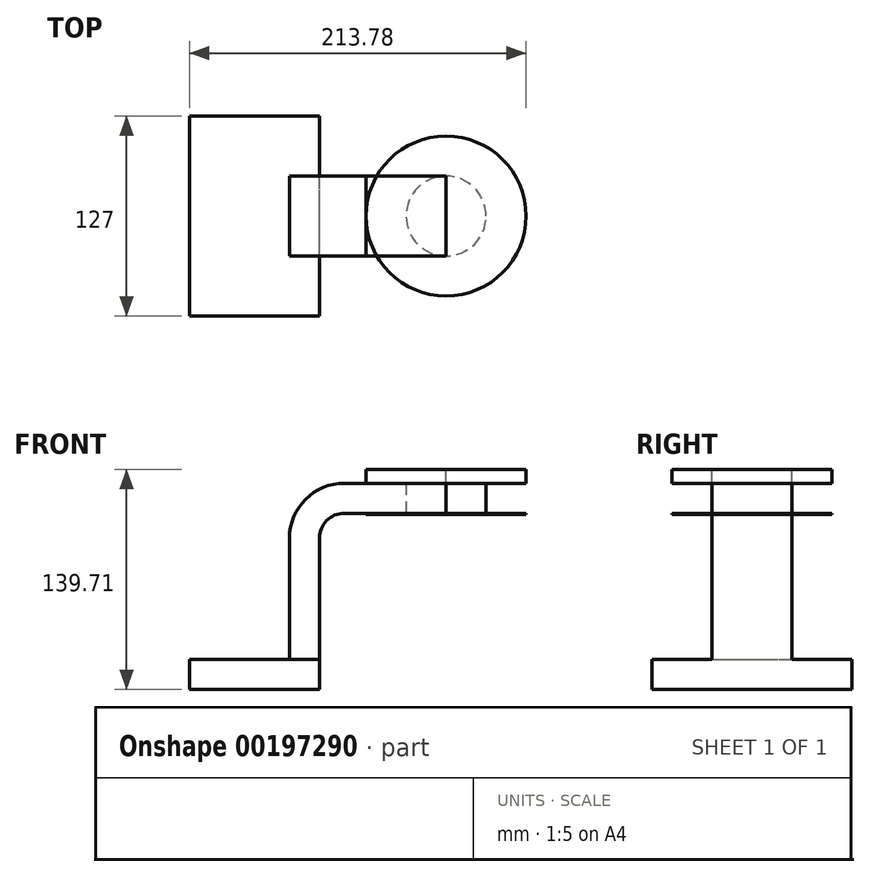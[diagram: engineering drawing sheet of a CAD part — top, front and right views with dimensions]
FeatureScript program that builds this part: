
annotation { "Feature Type Name" : "Feature", "Feature Type Description" : "" }
export const myFeature = defineFeature(function(context is Context, id is Id, definition is map)
    precondition{}
    {
        {
            var Q0;
            Q0=qCreatedBy(makeId("Front.planeOp"),FACE);
            var sketch = newSketch(context, id + "F0", { "sketchPlane" : qUnion([Q0])});
            skLineSegment(sketch, "E0.bottom", {"start": v(41.27, 9.53) * mm, "end": v(-41.27, 9.53) * mm});
            skLineSegment(sketch, "E0.top", {"start": v(41.28, -9.52) * mm, "end": v(-41.27, -9.52) * mm});
            skLineSegment(sketch, "E0.left", {"start": v(41.27, 9.53) * mm, "end": v(41.28, -9.52) * mm});
            skLineSegment(sketch, "E0.right", {"start": v(-41.27, 9.53) * mm, "end": v(-41.27, -9.52) * mm});
            skPoint(sketch, "E0.middle", {"position": v(0, 0) * mm});
            skLineSegment(sketch, "E1.bottom", {"start": v(121.7, 101.6) * mm, "end": v(70.9, 101.6) * mm});
            skLineSegment(sketch, "E1.top", {"start": v(121.7, 130.18) * mm, "end": v(70.9, 130.18) * mm});
            skLineSegment(sketch, "E1.left", {"start": v(121.7, 101.6) * mm, "end": v(121.7, 130.18) * mm});
            skLineSegment(sketch, "E1.right", {"start": v(70.9, 101.6) * mm, "end": v(70.9, 130.18) * mm});
            skPoint(sketch, "E1.middle", {"position": v(96.3, 115.89) * mm});
            skLineSegment(sketch, "E2", {"start": v(41.27, 9.53) * mm, "end": v(41.27, 86.54) * mm});
            skArc(sketch, "E3", {"start": v(41.27, 86.54) * mm, "mid": v(45.92, 97.77) * mm, "end": v(57.15, 102.42) * mm});
            skLineSegment(sketch, "E4", {"start": v(57.15, 102.42) * mm, "end": v(96.3, 102.42) * mm});
            skLineSegment(sketch, "E5.0", {"start": v(57.15, 121.47) * mm, "end": v(96.3, 121.47) * mm});
            skArc(sketch, "E5.1", {"start": v(22.22, 86.54) * mm, "mid": v(32.45, 111.24) * mm, "end": v(57.15, 121.47) * mm});
            skLineSegment(sketch, "E5.2", {"start": v(22.22, 9.53) * mm, "end": v(22.22, 86.54) * mm});
            skLineSegment(sketch, "E6", {"start": v(96.3, 121.47) * mm, "end": v(96.3, 102.42) * mm});
            skFitSpline(sketch, "E7", {"points": [v(-41.28, 9.53) * mm, v(57.15, 121.47) * mm], "startDerivative": vector(0.72, 245.98) * mm, "endDerivative": vector(63.18, -1.79) * mm});
            skSolve(sketch);
        }
        {
            var Q0;
            Q0=makeQuery(id+"F0.imprint","IMPRINT",FACE,{"disambiguationData":[TD([[makeQuery(id+"F0.imprint","IMPRINT",EDGE,{"derivedFrom":sQuery(id+"F0.wireOp",EDGE,"E0.top")}),-1.0]])]});
            extrude(context, id + "F1", {"entities" : qUnion([Q0]), "endBound" : BoundingType.SYMMETRIC, "depth" : 127 * mm});
        }
        {
            var Q0;
            {var subQ1=sQuery(id+"F0.wireOp",EDGE,"E2");Q0=makeQuery(id+"F0.imprint","IMPRINT",FACE,{"disambiguationData":[TD([[makeQuery(id+"F0.imprint","IMPRINT",EDGE,{"derivedFrom":subQ1}),1.0]])]});}
            var Q1;
            {var subQ1=sQuery(id+"F0.wireOp",EDGE,"E1.bottom");Q1=makeQuery(id+"F0.imprint","IMPRINT",FACE,{"disambiguationData":[TD([[makeQuery(id+"F0.imprint","IMPRINT",EDGE,{"derivedFrom":subQ1}),-1.0]])]});}
            var Q2;
            {var subQ5=sQuery(id+"F0.wireOp",EDGE,"E6");Q2=makeQuery(id+"F0.imprint","IMPRINT",FACE,{"disambiguationData":[TD([[makeQuery(id+"F0.imprint","IMPRINT",EDGE,{"derivedFrom":subQ5}),-1.0]])]});}
            extrude(context, id + "F2", {"entities" : qUnion([Q0, Q1, Q2]), "operationType" : NewBodyOperationType.ADD, "endBound" : BoundingType.SYMMETRIC, "depth" : 50.8 * mm});
        }
        {
            var Q0;
            Q0=makeQuery(id+"F0.imprint","IMPRINT",FACE,{"disambiguationData":[TD([[makeQuery(id+"F0.imprint","IMPRINT",EDGE,{"derivedFrom":sQuery(id+"F0.wireOp",EDGE,"E5.1")}),1.0]])]});
            extrude(context, id + "F3", {"entities" : qUnion([Q0]), "operationType" : NewBodyOperationType.ADD, "endBound" : BoundingType.SYMMETRIC, "depth" : 15.88 * mm});
        }
        {
            var Q0;
            {var subQ1=sQuery(id+"F0.wireOp",EDGE,"E1.bottom");Q0=makeQuery(id+"F0.imprint","IMPRINT",FACE,{"disambiguationData":[TD([[makeQuery(id+"F0.imprint","IMPRINT",EDGE,{"derivedFrom":subQ1}),-1.0]])]});}
            var Q1;
            Q1=sQuery(id+"F0.wireOp",EDGE,"E1.left");
            revolve(context, id + "F4", {"entities" : qUnion([Q0]), "axis" : qUnion([Q1]), "revolveType" : RevolveType.FULL});
        }
    });
